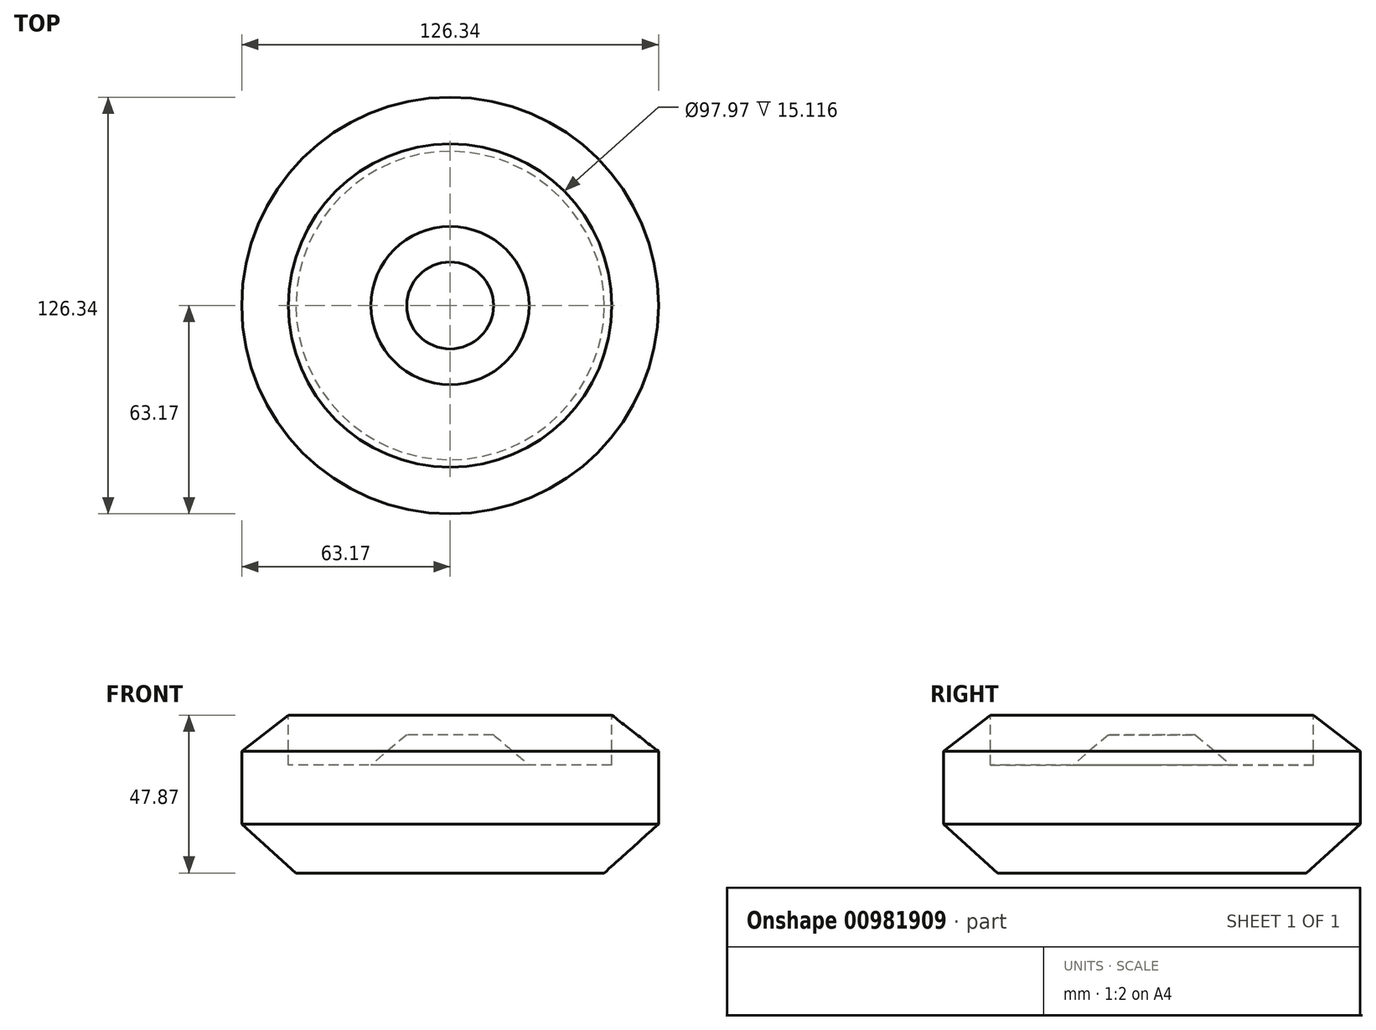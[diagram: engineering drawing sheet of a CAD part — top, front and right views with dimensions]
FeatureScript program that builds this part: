
annotation { "Feature Type Name" : "Feature", "Feature Type Description" : "" }
export const myFeature = defineFeature(function(context is Context, id is Id, definition is map)
    precondition{}
    {
        {
            var Q0;
            Q0=qCreatedBy(makeId("Front.planeOp"),FACE);
            var sketch = newSketch(context, id + "F0", { "sketchPlane" : qUnion([Q0])});
            skLineSegment(sketch, "E0", {"start": v(0, 0) * mm, "end": v(46.75, 0) * mm});
            skLineSegment(sketch, "E1", {"start": v(46.75, 0) * mm, "end": v(63.17, 14.84) * mm});
            skLineSegment(sketch, "E2", {"start": v(63.17, 14.84) * mm, "end": v(63.17, 36.86) * mm});
            skLineSegment(sketch, "E3", {"start": v(63.17, 36.86) * mm, "end": v(48.99, 47.87) * mm});
            skLineSegment(sketch, "E4", {"start": v(48.99, 47.87) * mm, "end": v(48.99, 32.75) * mm});
            skLineSegment(sketch, "E5", {"start": v(48.99, 32.75) * mm, "end": v(23.98, 32.75) * mm});
            skLineSegment(sketch, "E6", {"start": v(23.98, 32.75) * mm, "end": v(13.16, 41.9) * mm});
            skLineSegment(sketch, "E7", {"start": v(13.16, 41.9) * mm, "end": v(0, 41.9) * mm});
            skLineSegment(sketch, "E8", {"start": v(0, 41.9) * mm, "end": v(0, 0) * mm});
            skSolve(sketch);
        }
        {
            var Q0;
            Q0=makeQuery(id+"F0.imprint","IMPRINT",FACE,{"disambiguationData":[TD([[makeQuery(id+"F0.imprint","IMPRINT",EDGE,{"derivedFrom":sQuery(id+"F0.wireOp",EDGE,"E0")}),1.0]])]});
            var Q1;
            Q1=sQuery(id+"F0.wireOp",EDGE,"E8");
            revolve(context, id + "F1", {"surfaceOperationType" : NewSurfaceOperationType.NEW, "entities" : qUnion([Q0]), "axis" : qUnion([Q1]), "revolveType" : RevolveType.FULL});
        }
    });
